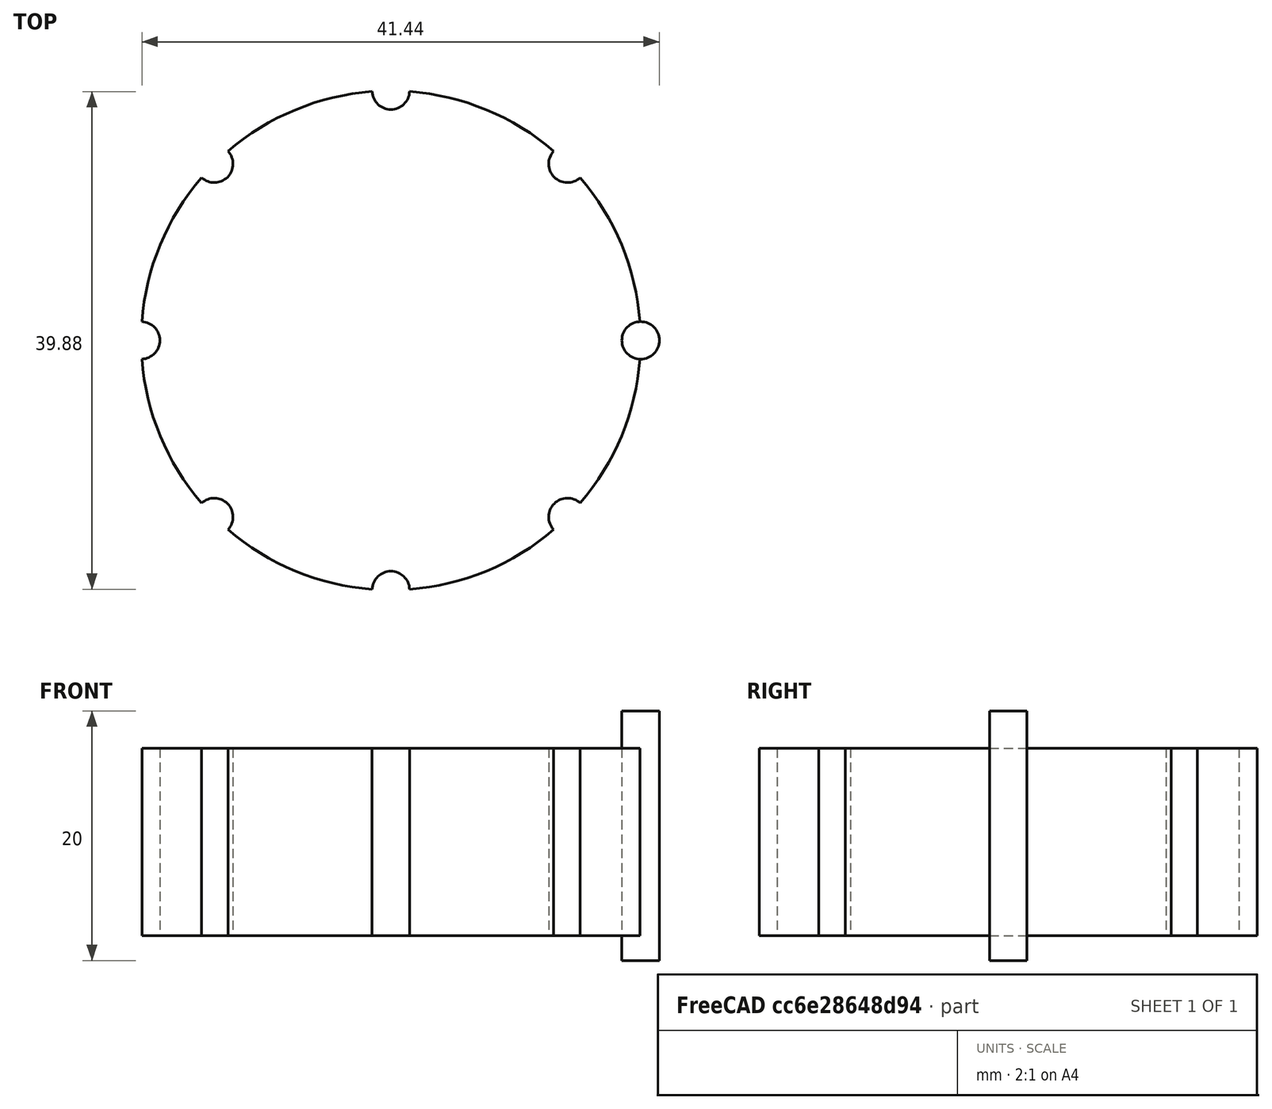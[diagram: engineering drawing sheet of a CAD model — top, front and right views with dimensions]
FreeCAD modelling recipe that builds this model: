
FCSTD DOCUMENT  (FreeCAD 0.20R29603 (Git))
Label: OJT1_T04R07_boto
License: All rights reserved
LicenseURL: http://en.wikipedia.org/wiki/All_rights_reserved
objects: Part::Cylinder×2, Part::FeaturePython×1, Part::Cut×1
note: 3 computed .brp shape members not serialized (recipe doc carries the construction recipe); baked Part::Feature solids carry a one-line shape summary decoded from their .brp

FEATURE [Part::Cylinder] Cylinder  label="Cilindre"
  Angle = 360
  AttacherType = Attacher::AttachEngine3D
  FirstAngle = 0
  Height = 15
  Radius = 20
  SecondAngle = 0
FEATURE [Part::Cylinder] Cylinder001  label="Resta"
  Angle = 360
  AttacherType = Attacher::AttachEngine3D
  FirstAngle = 0
  Height = 20
  Placement = pos=(20,0,-2) rot=(0,0,1;0rad)
  Radius = 1.5
  SecondAngle = 0
FEATURE [Part::FeaturePython] Array  # Draft array (typed FeaturePython)
  AlwaysSyncPlacement = false
  Angle = 360
  ArrayType = 1
  Axis = (0,0,1)
  Base = -> Cylinder001
  Center = (0,0,0)
  Count = 8
  ExpandArray = false
  Fuse = false
  IntervalAxis = (0,0,0)
  IntervalX = (50,0,0)
  IntervalY = (0,50,0)
  IntervalZ = (0,0,50)
  NumberCircles = 3
  NumberPolar = 8
  NumberX = 2
  NumberY = 2
  NumberZ = 1
  PlacementList = 8 placements: [(20,0,-2),(14.1421,14.1421,-2),(0,20,-2),(-14.1421,14.1421,-2),(-20,2.44929e-15,-2),(-14.1421,-14.1421,-2),(-3.55271e-15,-20,-2),(14.1421,-14.1421,-2)]
  RadialDistance = 50
  ScaleList = (8) [(1,1,1),(1,1,1),(1,1,1),(1,1,1),(1,1,1),(1,1,1),(1,1,1),(1,1,1)]
  Symmetry = 1
  TangentialDistance = 25
FEATURE [Part::Cut] Cut
  Base = -> Cylinder
  Tool = -> Array
